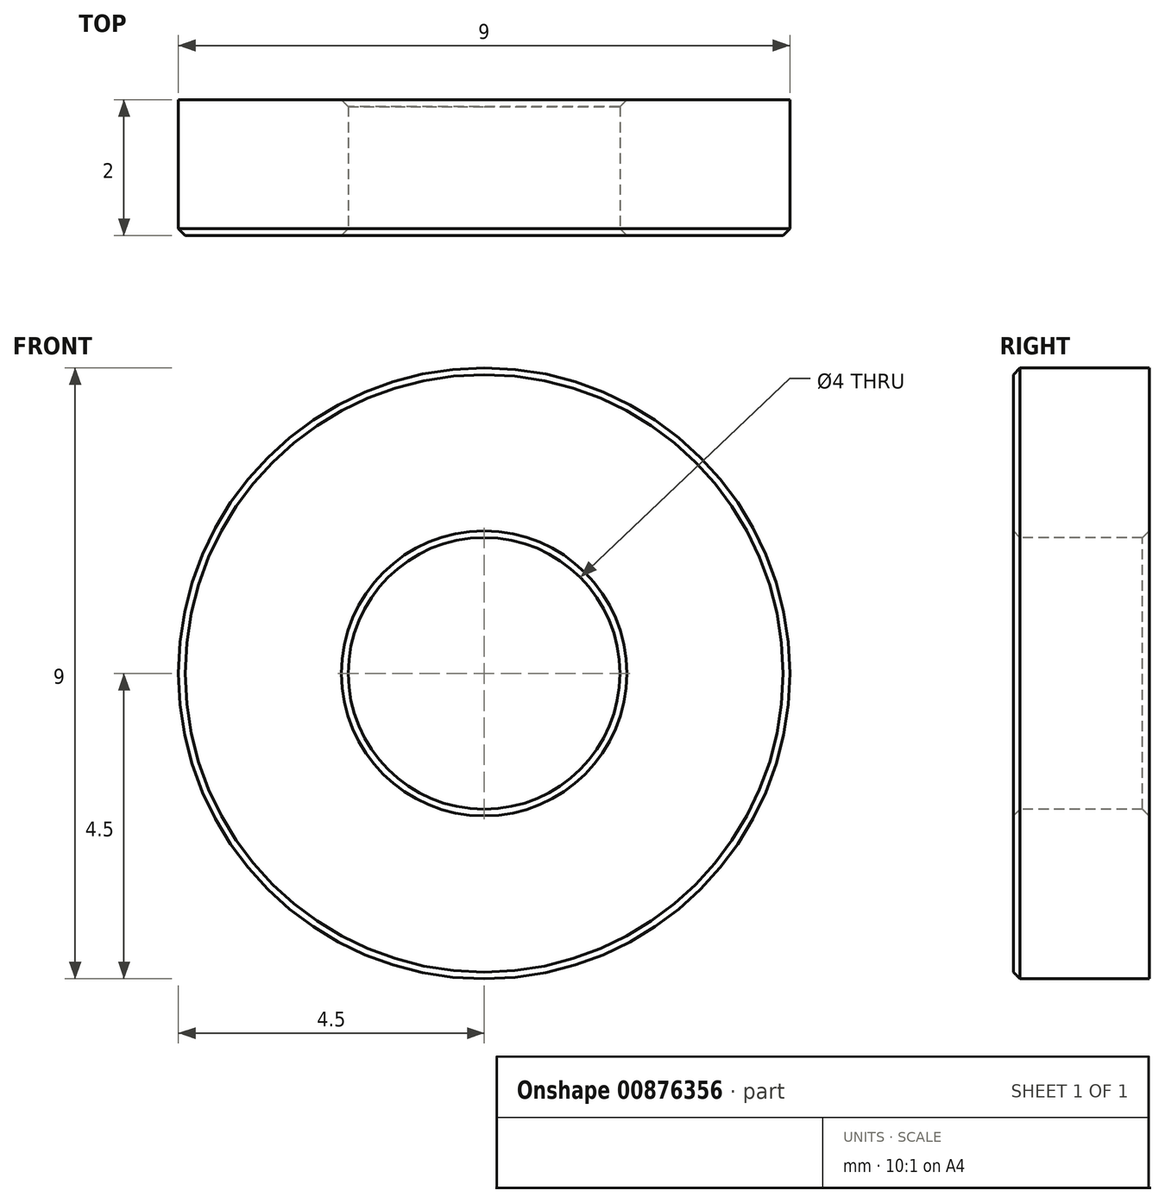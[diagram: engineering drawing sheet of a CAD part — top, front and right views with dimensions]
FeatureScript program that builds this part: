
annotation { "Feature Type Name" : "Feature", "Feature Type Description" : "" }
export const myFeature = defineFeature(function(context is Context, id is Id, definition is map)
    precondition{}
    {
        {
            var Q0;
            Q0=qCreatedBy(makeId("Front.planeOp"),FACE);
            var sketch = newSketch(context, id + "F0", { "sketchPlane" : qUnion([Q0])});
            skCircle(sketch, "E0", {"center": v(0, 0) * mm, "radius": 4.5 * mm});
            skSolve(sketch);
        }
        {
            var Q0;
            Q0 = qSketchRegion(id + "F0", true);
            extrude(context, id + "F1", {"entities" : qUnion([Q0]), "oppositeDirection" : true, "depth" : 2 * mm, "offsetDistance" : 25 * mm});
        }
        {
            var Q0;
            Q0=makeQuery(id+"F1.opExtrude","CAP_FACE",FACE,{"disambiguationData":[OSD([sQuery(id+"F0.wireOp",EDGE,"E0")])],"isStart":true});
            var sketch = newSketch(context, id + "F2", { "sketchPlane" : qUnion([Q0])});
            skCircle(sketch, "E1", {"center": v(0, 0) * mm, "radius": 2 * mm});
            skSolve(sketch);
        }
        {
            var Q0;
            Q0 = qSketchRegion(id + "F2", true);
            extrude(context, id + "F3", {"entities" : qUnion([Q0]), "operationType" : NewBodyOperationType.REMOVE, "endBound" : BoundingType.THROUGH_ALL, "oppositeDirection" : true, "depth" : 25 * mm, "offsetDistance" : 25 * mm});
        }
        {
            var Q0;
            Q0=makeQuery(id+"F3.boolean.opBoolean","COPY",EDGE,{"derivedFrom":makeQuery(id+"F3.opExtrude","CAP_EDGE",EDGE,{"disambiguationData":[OSD([sQuery(id+"F2.wireOp",EDGE,"E1")])],"isStart":true})});
            var Q1;
            Q1=makeQuery(id+"F1.opExtrude","CAP_FACE",FACE,{"disambiguationData":[OSD([sQuery(id+"F0.wireOp",EDGE,"E0")])],"isStart":true});
            var Q2;
            Q2=makeQuery(id+"F3.boolean.opBoolean","INTERSECT",EDGE,{"derivedFrom":[makeQuery(id+"F1.opExtrude","CAP_FACE",FACE,{"disambiguationData":[OSD([sQuery(id+"F0.wireOp",EDGE,"E0")])],"isStart":false}),makeQuery(id+"F3.opExtrude","SWEPT_FACE",FACE,{"disambiguationData":[OSD([sQuery(id+"F2.wireOp",EDGE,"E1")])]})]});
            chamfer(context, id + "F4", {"entities" : qUnion([Q0, Q1, Q2]), "width" : 0.1 * mm, "tangentPropagation" : true});
        }
    });
